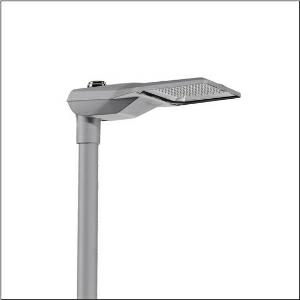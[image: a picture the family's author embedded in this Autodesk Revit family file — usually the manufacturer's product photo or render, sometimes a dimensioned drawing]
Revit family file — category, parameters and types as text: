
# Revit family: streetlight_sl_21_midi___pl52_5xe7h47n08lb_ccfd
name_source: partatom
category: Lighting Fixtures
units: mm (PartAtom-declared; Revit-internal decimal feet)

## family parameters
Cut with Voids When Loaded = No
Host = Face
Light Source = No
Part Type = Normal
Room Calculation Point = No
Round Connector Dimension = Use Diameter
Shared = No

## types (1)
- --- (1 x LED, 14690 lm, 98.3 W, 4000K)
    Apparent Load = 98 VA
    CIE Flux Codes = 27 59 98 100 100
    Color Rendering = 70
    Color Temperature = 4000K
    Default Elevation = 1800 mm
    Description = Streetlight SL 21 midi, mast luminaire, primary light control with lens, of PMMA, primary optical cover: cover, of toughened safety glass, transparent, light distribution: PL52, light emission: direct distribution, primary light characteristic: asymmetric, installation type: side-entry, LED, 3G 2.5mm², High Power LED, rated luminous flux: 14.690lm, luminous efficacy: 149lm/W, light colour: 740, colour temperature: 4000K, control gear: NEMA (7pin), control: overheat protection, pre-setting: linear dimming characteristic, constant luminous flux control, time-dependent luminous flux control, flexible luminous flux parameterisation, mains connection: 220..240V, AC, 50/60Hz, connection cable pre-assembled, cable length: 10,5m, wiring characteristics: H05VV-F, start of lifetime: 98W, end of service life: 101W, reduction: 45W, luminaire housing, of diecast aluminium (EN AC-44300), powder-coated, SITECO metallic grey (DB 702S), corrosivity category C5 high according to DIN EN ISO 12944, multi-level sealing system, sealing non-destructively replaceable, inclination adjustable: 0°, 5°, 10°, 15°, length: 644mm, width: 335mm, height: 110mm, spigot size: 42mm (side-entry), mounting height: 4..8m, protection rating (complete): IP66, insulation class (complete): insulation class I (protective earthing), certification: CE, ENEC, ENEC+, VDE, impact resistance: IK10, permissible operating ambient temperature for outdoor applications: -40..+50°C, standard-compliant lighting for roads and squares, packaging unit: 1 piece

Light Distribution: PL52
    Height = 111 mm
    Lamp = 1 x LED
    Lamp Light Flux = 14690 lm
    Lamp Power = 98.3 W
    Lamp count = 1
    Length = 644 mm
    Luminous efficacy = 149 lm/W
    Manufacturer = Siteco
    ModVariant = No
    Model = 5XE7H47N08LB
    Number of Poles = 1
    OnlyDefault = Yes
    Power Factor = 1
    Product Name = Streetlight SL 21 midi | PL52
    Product group = mast luminaire | pylon top
    ProductGroupID = 6100
    Protection Class = Protection class I
    Protection Degree = IP 66
    RLX_Detail_Level = 1
    RLX_Emergency_Light_Flux = 0 lm
    RLX_Emergency_Type = 0
    RLX_Emergency_Type_DB = No
    RlxData = <blob elided: 36281 chars, md5=d868f37b>
    Socket = socket
    Standby Power = 0 W
    System Light Flux = 14690 lm
    System Power = 98 W
    Type Comments = factory setting: luminous flux: 100 % | dim-lin: 254 | 1020 mA
    Type Image = l_1294377.jpg
    URL = http://relux.com
    VarID = @adj_136343
    Voltage = 0 V
    Weight = 0.00 kg
    Width = 336 mm

## geometry (parser evidence)
native form markers: Blend x4, Sweep x9
no freeform markers — native parametric forms only
